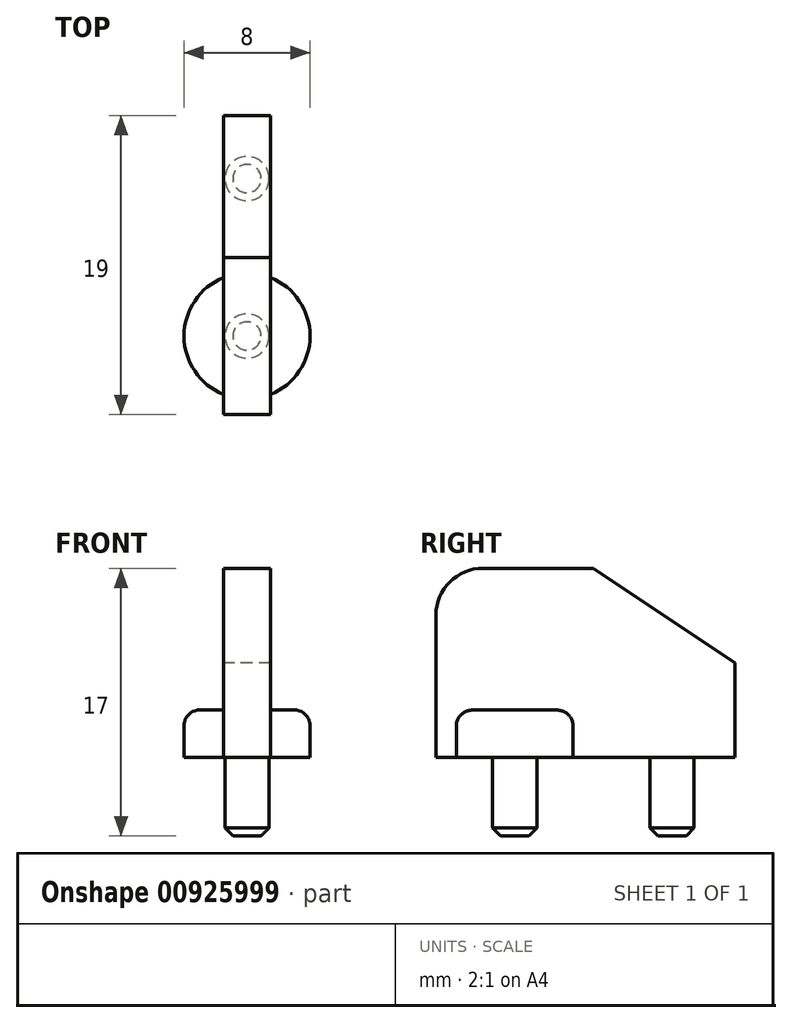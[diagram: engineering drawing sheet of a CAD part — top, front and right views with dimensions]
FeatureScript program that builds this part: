
annotation { "Feature Type Name" : "Feature", "Feature Type Description" : "" }
export const myFeature = defineFeature(function(context is Context, id is Id, definition is map)
    precondition{}
    {
        {
            var Q0;
            Q0=qCreatedBy(makeId("Top.planeOp"),FACE);
            var sketch = newSketch(context, id + "F0", { "sketchPlane" : qUnion([Q0])});
            skCircle(sketch, "E0", {"center": v(0, 5) * mm, "radius": 1.4 * mm});
            skCircle(sketch, "E1", {"center": v(0, -5) * mm, "radius": 1.4 * mm});
            skLineSegment(sketch, "E2.bottom", {"start": v(-1.5, 9) * mm, "end": v(1.5, 9) * mm});
            skLineSegment(sketch, "E2.top", {"start": v(-1.5, -10) * mm, "end": v(1.5, -10) * mm});
            skLineSegment(sketch, "E2.left", {"start": v(-1.5, 9) * mm, "end": v(-1.5, -10) * mm});
            skLineSegment(sketch, "E2.right", {"start": v(1.5, 9) * mm, "end": v(1.5, -10) * mm});
            skPoint(sketch, "E3.orphan", {"position": v(0, 9) * mm});
            skPoint(sketch, "E4.end.orphan", {"position": v(0, -10) * mm});
            skArc(sketch, "E5", {"start": v(1.5, -8.7) * mm, "mid": v(4, -5) * mm, "end": v(1.5, -1.3) * mm});
            skArc(sketch, "E6", {"start": v(1.5, 1.3) * mm, "mid": v(0, 9) * mm, "end": v(-1.5, 1.3) * mm});
            skArc(sketch, "E7.trimOffspring", {"start": v(-1.5, -1.3) * mm, "mid": v(-4, -5) * mm, "end": v(-1.5, -8.7) * mm});
            skSolve(sketch);
        }
        {
            var Q0;
            {var subQ5=sQuery(id+"F0.wireOp",EDGE,"E2.bottom");Q0=makeQuery(id+"F0.imprint","IMPRINT",FACE,{"disambiguationData":[TD([[makeQuery(id+"F0.imprint","IMPRINT",EDGE,{"derivedFrom":subQ5}),-1.0]])]});}
            var Q1;
            {var subQ0=sQuery(id+"F0.wireOp",EDGE,"E2.left");var subQ1=sQuery(id+"F0.wireOp",EDGE,"E0");var subQ2=makeQuery(id+"F0.imprint","INTERSECT",VERTEX,{"derivedFrom":[subQ1,subQ0]});Q1=makeQuery(id+"F0.imprint","IMPRINT",FACE,{"disambiguationData":[TD([[makeQuery(id+"F0.imprint","IMPRINT",EDGE,{"disambiguationData":[TD([[subQ2,-1.0]])],"derivedFrom":subQ1}),-1.0]])]});}
            var Q2;
            {var subQ5=sQuery(id+"F0.wireOp",EDGE,"E2.top");Q2=makeQuery(id+"F0.imprint","IMPRINT",FACE,{"disambiguationData":[TD([[makeQuery(id+"F0.imprint","IMPRINT",EDGE,{"derivedFrom":subQ5}),1.0]])]});}
            var Q3;
            {var subQ0=sQuery(id+"F0.wireOp",EDGE,"E1");var subQ1=makeQuery(id+"F0.imprint","INTERSECT",VERTEX,{"derivedFrom":[subQ0,sQuery(id+"F0.wireOp",EDGE,"E2.left")]});Q3=makeQuery(id+"F0.imprint","IMPRINT",FACE,{"disambiguationData":[TD([[makeQuery(id+"F0.imprint","IMPRINT",EDGE,{"disambiguationData":[TD([[subQ1,1.0]])],"derivedFrom":subQ0}),1.0]])]});}
            var Q4;
            {var subQ0=sQuery(id+"F0.wireOp",EDGE,"E0");var subQ1=makeQuery(id+"F0.imprint","INTERSECT",VERTEX,{"derivedFrom":[subQ0,sQuery(id+"F0.wireOp",EDGE,"E2.left")]});Q4=makeQuery(id+"F0.imprint","IMPRINT",FACE,{"disambiguationData":[TD([[makeQuery(id+"F0.imprint","IMPRINT",EDGE,{"disambiguationData":[TD([[subQ1,1.0]])],"derivedFrom":subQ0}),1.0]])]});}
            extrude(context, id + "F1", {"entities" : qUnion([Q0, Q1, Q2, Q3, Q4]), "depth" : 12 * mm, "offsetDistance" : 25 * mm});
        }
        {
            var Q0;
            {var subQ0=sQuery(id+"F0.wireOp",EDGE,"E0");var subQ1=makeQuery(id+"F0.imprint","INTERSECT",VERTEX,{"derivedFrom":[subQ0,sQuery(id+"F0.wireOp",EDGE,"E2.left")]});Q0=makeQuery(id+"F0.imprint","IMPRINT",FACE,{"disambiguationData":[TD([[makeQuery(id+"F0.imprint","IMPRINT",EDGE,{"disambiguationData":[TD([[subQ1,1.0]])],"derivedFrom":subQ0}),1.0]])]});}
            var Q1;
            {var subQ0=sQuery(id+"F0.wireOp",EDGE,"E1");var subQ1=makeQuery(id+"F0.imprint","INTERSECT",VERTEX,{"derivedFrom":[subQ0,sQuery(id+"F0.wireOp",EDGE,"E2.left")]});Q1=makeQuery(id+"F0.imprint","IMPRINT",FACE,{"disambiguationData":[TD([[makeQuery(id+"F0.imprint","IMPRINT",EDGE,{"disambiguationData":[TD([[subQ1,1.0]])],"derivedFrom":subQ0}),1.0]])]});}
            extrude(context, id + "F2", {"entities" : qUnion([Q0, Q1]), "operationType" : NewBodyOperationType.ADD, "oppositeDirection" : true, "depth" : 5 * mm, "offsetDistance" : 25 * mm});
        }
        {
            var Q0;
            Q0=makeQuery(id+"F2.opExtrude","CAP_EDGE",EDGE,{"disambiguationData":[OSD([sQuery(id+"F0.wireOp",EDGE,"E1")])],"isStart":false});
            var Q1;
            Q1=makeQuery(id+"F2.opExtrude","CAP_EDGE",EDGE,{"disambiguationData":[OSD([sQuery(id+"F0.wireOp",EDGE,"E0")])],"isStart":false});
            chamfer(context, id + "F3", {"entities" : qUnion([Q0, Q1]), "width" : 0.5 * mm, "tangentPropagation" : true});
        }
        {
            var Q0;
            {var subQ0=sQuery(id+"F0.wireOp",EDGE,"E7.trimOffspring");Q0=makeQuery(id+"F0.imprint","IMPRINT",FACE,{"disambiguationData":[TD([[makeQuery(id+"F0.imprint","IMPRINT",EDGE,{"derivedFrom":subQ0}),1.0]])]});}
            var Q1;
            {var subQ0=sQuery(id+"F0.wireOp",EDGE,"E6");var subQ1=sQuery(id+"F0.wireOp",EDGE,"E2.left");var subQ2=makeQuery(id+"F0.imprint","INTERSECT",VERTEX,{"disambiguationData":[OD(0.0)],"derivedFrom":[subQ1,subQ0]});Q1=makeQuery(id+"F0.imprint","IMPRINT",FACE,{"disambiguationData":[TD([[makeQuery(id+"F0.imprint","IMPRINT",EDGE,{"disambiguationData":[TD([[subQ2,1.0]])],"derivedFrom":subQ1}),-1.0]])]});}
            var Q2;
            {var subQ0=sQuery(id+"F0.wireOp",EDGE,"E5");Q2=makeQuery(id+"F0.imprint","IMPRINT",FACE,{"disambiguationData":[TD([[makeQuery(id+"F0.imprint","IMPRINT",EDGE,{"derivedFrom":subQ0}),1.0]])]});}
            var Q3;
            {var subQ0=sQuery(id+"F0.wireOp",EDGE,"E6");var subQ1=sQuery(id+"F0.wireOp",EDGE,"E2.right");var subQ2=makeQuery(id+"F0.imprint","INTERSECT",VERTEX,{"disambiguationData":[OD(0.0)],"derivedFrom":[subQ1,subQ0]});Q3=makeQuery(id+"F0.imprint","IMPRINT",FACE,{"disambiguationData":[TD([[makeQuery(id+"F0.imprint","IMPRINT",EDGE,{"disambiguationData":[TD([[subQ2,1.0]])],"derivedFrom":subQ1}),1.0]])]});}
            extrude(context, id + "F4", {"entities" : qUnion([Q0, Q1, Q2, Q3]), "operationType" : NewBodyOperationType.ADD, "depth" : 3 * mm, "offsetDistance" : 25 * mm});
        }
        {
            var Q0;
            {var subQ0=sQuery(id+"F0.wireOp",EDGE,"E6");var subQ1=sQuery(id+"F0.wireOp",EDGE,"E2.left");Q0=makeQuery(id+"F4.opExtrude","CAP_EDGE",EDGE,{"disambiguationData":[OSD([subQ0]),TDD([makeQuery(id+"F0.imprint","IMPRINT",EDGE,{"disambiguationData":[TD([[makeQuery(id+"F0.imprint","INTERSECT",VERTEX,{"disambiguationData":[OD(0.0)],"derivedFrom":[subQ1,subQ0]}),1.0]])],"derivedFrom":subQ0})])],"isStart":false});}
            var Q1;
            Q1=makeQuery(id+"F4.opExtrude","CAP_EDGE",EDGE,{"disambiguationData":[OSD([sQuery(id+"F0.wireOp",EDGE,"E7.trimOffspring")])],"isStart":false});
            var Q2;
            Q2=makeQuery(id+"F4.opExtrude","CAP_EDGE",EDGE,{"disambiguationData":[OSD([sQuery(id+"F0.wireOp",EDGE,"E5")])],"isStart":false});
            var Q3;
            {var subQ0=sQuery(id+"F0.wireOp",EDGE,"E6");var subQ1=sQuery(id+"F0.wireOp",EDGE,"E2.right");Q3=makeQuery(id+"F4.opExtrude","CAP_EDGE",EDGE,{"disambiguationData":[OSD([subQ0]),TDD([makeQuery(id+"F0.imprint","IMPRINT",EDGE,{"disambiguationData":[TD([[makeQuery(id+"F0.imprint","INTERSECT",VERTEX,{"disambiguationData":[OD(0.0)],"derivedFrom":[subQ1,subQ0]}),-1.0]])],"derivedFrom":subQ0})])],"isStart":false});}
            fillet(context, id + "F5", {"entities" : qUnion([Q0, Q1, Q2, Q3]), "radius" : 1 * mm, "tangentPropagation" : true, "allowEdgeOverflow" : false});
        }
        {
            var Q0;
            Q0=makeQuery(id+"F1.opExtrude","SWEPT_FACE",FACE,{"disambiguationData":[OSD([sQuery(id+"F0.wireOp",EDGE,"E2.left")])]});
            var sketch = newSketch(context, id + "F6", { "sketchPlane" : qUnion([Q0])});
            skLineSegment(sketch, "E8", {"start": v(-9, 12) * mm, "end": v(-9, 6) * mm});
            skLineSegment(sketch, "E9", {"start": v(0, 12) * mm, "end": v(-9, 6) * mm});
            skSolve(sketch);
        }
        {
            var Q0;
            Q0=qSketchRegion(id+"F6",true);
            var Q1;
            {var subQ0=sQuery(id+"F6.wireOp",EDGE,"E8");Q1=makeQuery(id+"F6.imprint","IMPRINT",FACE,{"disambiguationData":[TD([[makeQuery(id+"F6.imprint","IMPRINT",EDGE,{"derivedFrom":subQ0}),1.0]])]});}
            extrude(context, id + "F7", {"entities" : qUnion([Q0, Q1]), "operationType" : NewBodyOperationType.REMOVE, "oppositeDirection" : true, "depth" : 25 * mm, "offsetDistance" : 25 * mm});
        }
        {
            var Q0;
            Q0=makeQuery(id+"F1.opExtrude","CAP_EDGE",EDGE,{"disambiguationData":[OSD([sQuery(id+"F0.wireOp",EDGE,"E2.top")])],"isStart":false});
            var Q1;
            Q1=makeQuery(id+"F7.boolean.opBoolean","COPY",EDGE,{"derivedFrom":makeQuery(id+"F7.opExtrude","SWEPT_EDGE",EDGE,{"disambiguationData":[OSD([sQuery(id+"F0.wireOp",EDGE,"E2.left"),sQuery(id+"F6.wireOp",EDGE,"E9")])]})});
            var Q2;
            Q2=makeQuery(id+"F7.boolean.opBoolean","COPY",EDGE,{"derivedFrom":makeQuery(id+"F7.opExtrude","SWEPT_EDGE",EDGE,{"disambiguationData":[OSD([sQuery(id+"F0.wireOp",EDGE,"E2.bottom"),sQuery(id+"F0.wireOp",EDGE,"E2.left"),sQuery(id+"F6.wireOp",EDGE,"E8"),sQuery(id+"F6.wireOp",EDGE,"E9")])]})});
            fillet(context, id + "F8", {"entities" : qUnion([Q0, Q1, Q2]), "radius" : 3 * mm, "tangentPropagation" : true, "allowEdgeOverflow" : false});
        }
    });
